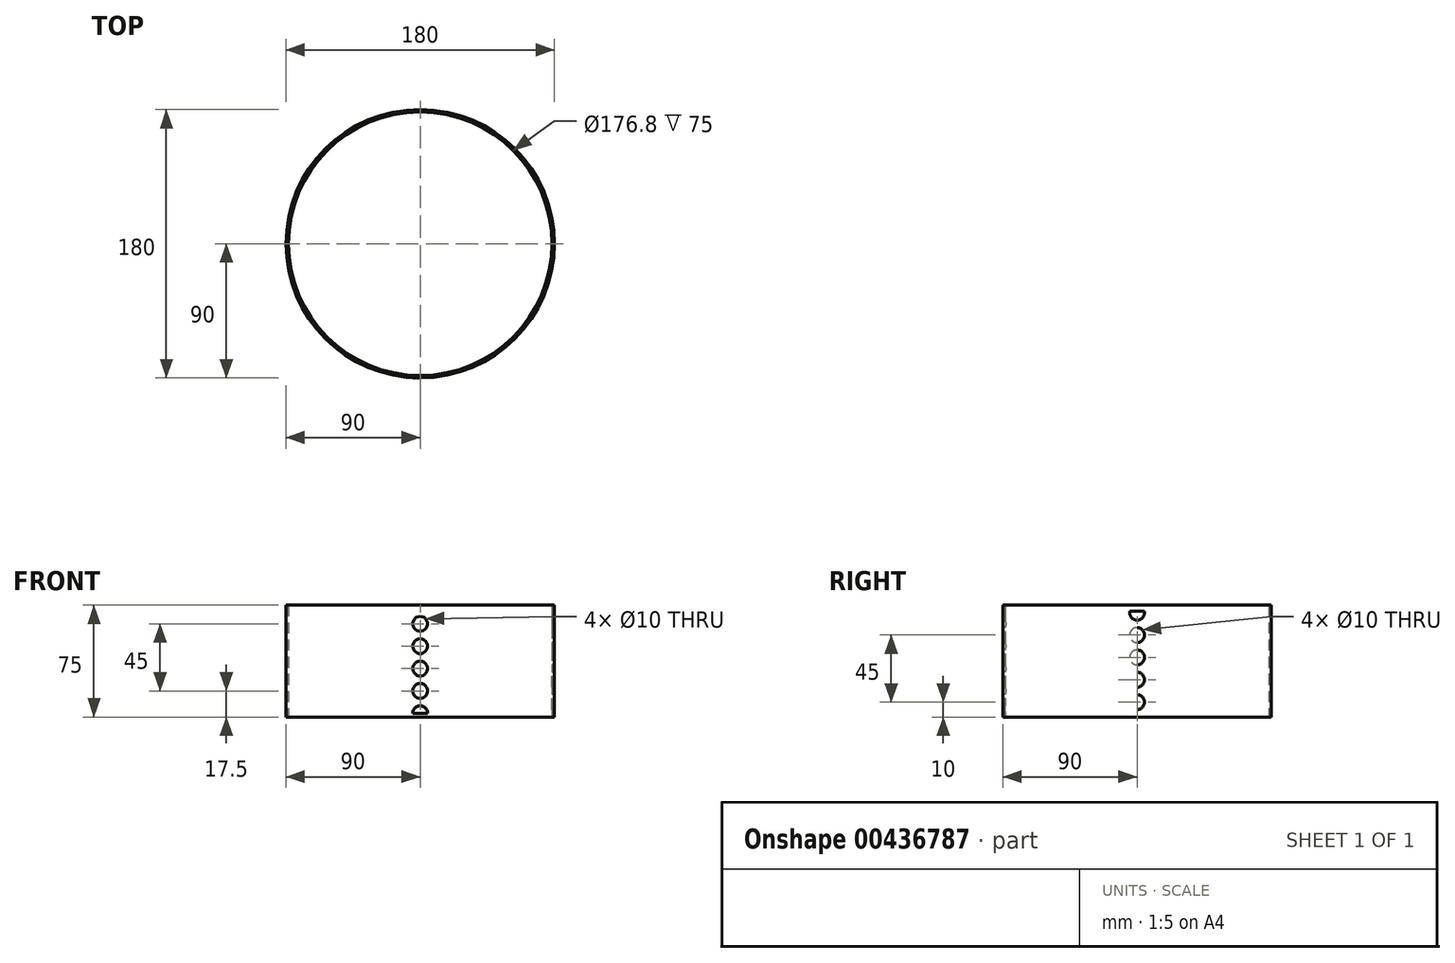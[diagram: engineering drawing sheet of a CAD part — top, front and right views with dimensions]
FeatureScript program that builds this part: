
annotation { "Feature Type Name" : "Feature", "Feature Type Description" : "" }
export const myFeature = defineFeature(function(context is Context, id is Id, definition is map)
    precondition{}
    {
        {
            var Q0;
            Q0=qCreatedBy(makeId("Top.planeOp"),FACE);
            var sketch = newSketch(context, id + "F0", { "sketchPlane" : qUnion([Q0])});
            skCircle(sketch, "E0", {"center": v(0, 0) * mm, "radius": 90 * mm});
            skSolve(sketch);
        }
        {
            var Q0;
            Q0 = qSketchRegion(id + "F0", true);
            var Q1;
            Q1=sQuery(id+"F0.wireOp",EDGE,"E0");
            extrude(context, id + "F1", {"entities" : qUnion([Q0]), "surfaceEntities" : qUnion([Q1]), "endBound" : BoundingType.SYMMETRIC, "depth" : 75 * mm});
        }
        {
            var Q0;
            Q0=makeQuery(id+"F1.opExtrude","CAP_FACE",FACE,{"disambiguationData":[OSD([sQuery(id+"F0.wireOp",EDGE,"E0")])],"isStart":false});
            shell(context, id + "F2", {"entities" : qUnion([Q0]), "thickness" : 1.6 * mm});
        }
        {
            var Q0;
            {var subQ0=sQuery(id+"F0.wireOp",EDGE,"E0");Q0=makeQuery(id+"F2.opShell","OFFSET_FACE",FACE,{"disambiguationData":[OSD([subQ0]),TDD([makeQuery(id+"F1.opExtrude","CAP_FACE",FACE,{"disambiguationData":[OSD([subQ0])],"isStart":true})])]});}
            var sketch = newSketch(context, id + "F3", { "sketchPlane" : qUnion([Q0])});
            skCircle(sketch, "E1", {"center": v(0, 0) * mm, "radius": 88.4 * mm});
            skSolve(sketch);
        }
        {
            var Q0;
            Q0 = qSketchRegion(id + "F3", true);
            extrude(context, id + "F4", {"entities" : qUnion([Q0]), "operationType" : NewBodyOperationType.REMOVE, "oppositeDirection" : true, "depth" : 25 * mm});
        }
        {
            var Q0;
            Q0=qCreatedBy(makeId("Right.planeOp"),FACE);
            cPlane(context, id + "F5", {"entities" : qUnion([Q0]), "cplaneType" : CPlaneType.OFFSET, "offset" : 83 * mm, "width" : 150 * mm, "height" : 150 * mm});
        }
        {
            var Q0;
            Q0=qCreatedBy(id+"F5.planeOp",FACE);
            var sketch = newSketch(context, id + "F6", { "sketchPlane" : qUnion([Q0])});
            skCircle(sketch, "E2", {"center": v(0, 32.5) * mm, "radius": 5 * mm});
            skCircle(sketch, "E3.0.1.0", {"center": v(0, 17.5) * mm, "radius": 5 * mm});
            skCircle(sketch, "E3.0.2.0", {"center": v(0, 2.5) * mm, "radius": 5 * mm});
            skCircle(sketch, "E3.0.3.0", {"center": v(0, -12.5) * mm, "radius": 5 * mm});
            skCircle(sketch, "E3.0.4.0", {"center": v(0, -27.5) * mm, "radius": 5 * mm});
            skLineSegment(sketch, "E3.direction1", {"start": v(0, 32.5) * mm, "end": v(25, 32.5) * mm, "construction": true});
            skLineSegment(sketch, "E3.direction2", {"start": v(0, 32.5) * mm, "end": v(0, 17.5) * mm, "construction": true});
            skLineSegment(sketch, "E4", {"start": v(-4.88, 33.58) * mm, "end": v(4.88, 33.58) * mm});
            skSolve(sketch);
        }
        {
            var Q0;
            Q0=makeQuery(id+"F6.imprint","IMPRINT",FACE,{"disambiguationData":[TD([[makeQuery(id+"F6.imprint","IMPRINT",EDGE,{"derivedFrom":sQuery(id+"F6.wireOp",EDGE,"E3.0.2.0")}),1.0]])]});
            var Q1;
            Q1=makeQuery(id+"F6.imprint","IMPRINT",FACE,{"disambiguationData":[TD([[makeQuery(id+"F6.imprint","IMPRINT",EDGE,{"derivedFrom":sQuery(id+"F6.wireOp",EDGE,"E3.0.1.0")}),1.0]])]});
            var Q2;
            Q2=makeQuery(id+"F6.imprint","IMPRINT",FACE,{"disambiguationData":[TD([[makeQuery(id+"F6.imprint","IMPRINT",EDGE,{"derivedFrom":sQuery(id+"F6.wireOp",EDGE,"E3.0.3.0")}),1.0]])]});
            var Q3;
            Q3=makeQuery(id+"F6.imprint","IMPRINT",FACE,{"disambiguationData":[TD([[makeQuery(id+"F6.imprint","IMPRINT",EDGE,{"derivedFrom":sQuery(id+"F6.wireOp",EDGE,"E3.0.4.0")}),1.0]])]});
            var Q4;
            {var subQ0=sQuery(id+"F6.wireOp",EDGE,"E4");Q4=makeQuery(id+"F6.imprint","IMPRINT",FACE,{"disambiguationData":[TD([[makeQuery(id+"F6.imprint","IMPRINT",EDGE,{"derivedFrom":subQ0}),-1.0]])]});}
            extrude(context, id + "F7", {"entities" : qUnion([Q0, Q1, Q2, Q3, Q4]), "operationType" : NewBodyOperationType.REMOVE, "depth" : 103 * mm});
        }
        {
            var Q0;
            Q0=qCreatedBy(makeId("Front.planeOp"),FACE);
            cPlane(context, id + "F8", {"entities" : qUnion([Q0]), "cplaneType" : CPlaneType.OFFSET, "offset" : 84.8 * mm, "width" : 150 * mm, "height" : 150 * mm});
        }
        {
            var Q0;
            Q0=qCreatedBy(id+"F8.planeOp",FACE);
            var sketch = newSketch(context, id + "F9", { "sketchPlane" : qUnion([Q0])});
            skCircle(sketch, "E5", {"center": v(0, -35) * mm, "radius": 5 * mm});
            skCircle(sketch, "E6.0.1.0", {"center": v(0, -20) * mm, "radius": 5 * mm});
            skCircle(sketch, "E6.0.2.0", {"center": v(0, -5) * mm, "radius": 5 * mm});
            skCircle(sketch, "E6.0.3.0", {"center": v(0, 10) * mm, "radius": 5 * mm});
            skCircle(sketch, "E6.0.4.0", {"center": v(0, 25) * mm, "radius": 5 * mm});
            skLineSegment(sketch, "E6.direction1", {"start": v(0, -35) * mm, "end": v(25, -35) * mm, "construction": true});
            skLineSegment(sketch, "E6.direction2", {"start": v(0, -35) * mm, "end": v(0, -20) * mm, "construction": true});
            skLineSegment(sketch, "E7", {"start": v(5, -35) * mm, "end": v(-5, -35) * mm});
            skSolve(sketch);
        }
        {
            var Q0;
            {var subQ0=sQuery(id+"F9.wireOp",EDGE,"E7");Q0=makeQuery(id+"F9.imprint","IMPRINT",FACE,{"disambiguationData":[TD([[makeQuery(id+"F9.imprint","IMPRINT",EDGE,{"derivedFrom":subQ0}),-1.0]])]});}
            var Q1;
            Q1=makeQuery(id+"F9.imprint","IMPRINT",FACE,{"disambiguationData":[TD([[makeQuery(id+"F9.imprint","IMPRINT",EDGE,{"derivedFrom":sQuery(id+"F9.wireOp",EDGE,"E6.0.1.0")}),1.0]])]});
            var Q2;
            Q2=makeQuery(id+"F9.imprint","IMPRINT",FACE,{"disambiguationData":[TD([[makeQuery(id+"F9.imprint","IMPRINT",EDGE,{"derivedFrom":sQuery(id+"F9.wireOp",EDGE,"E6.0.2.0")}),1.0]])]});
            var Q3;
            Q3=makeQuery(id+"F9.imprint","IMPRINT",FACE,{"disambiguationData":[TD([[makeQuery(id+"F9.imprint","IMPRINT",EDGE,{"derivedFrom":sQuery(id+"F9.wireOp",EDGE,"E6.0.3.0")}),1.0]])]});
            var Q4;
            Q4=makeQuery(id+"F9.imprint","IMPRINT",FACE,{"disambiguationData":[TD([[makeQuery(id+"F9.imprint","IMPRINT",EDGE,{"derivedFrom":sQuery(id+"F9.wireOp",EDGE,"E6.0.4.0")}),1.0]])]});
            extrude(context, id + "F10", {"entities" : qUnion([Q0, Q1, Q2, Q3, Q4]), "operationType" : NewBodyOperationType.REMOVE, "depth" : 25 * mm});
        }
    });
